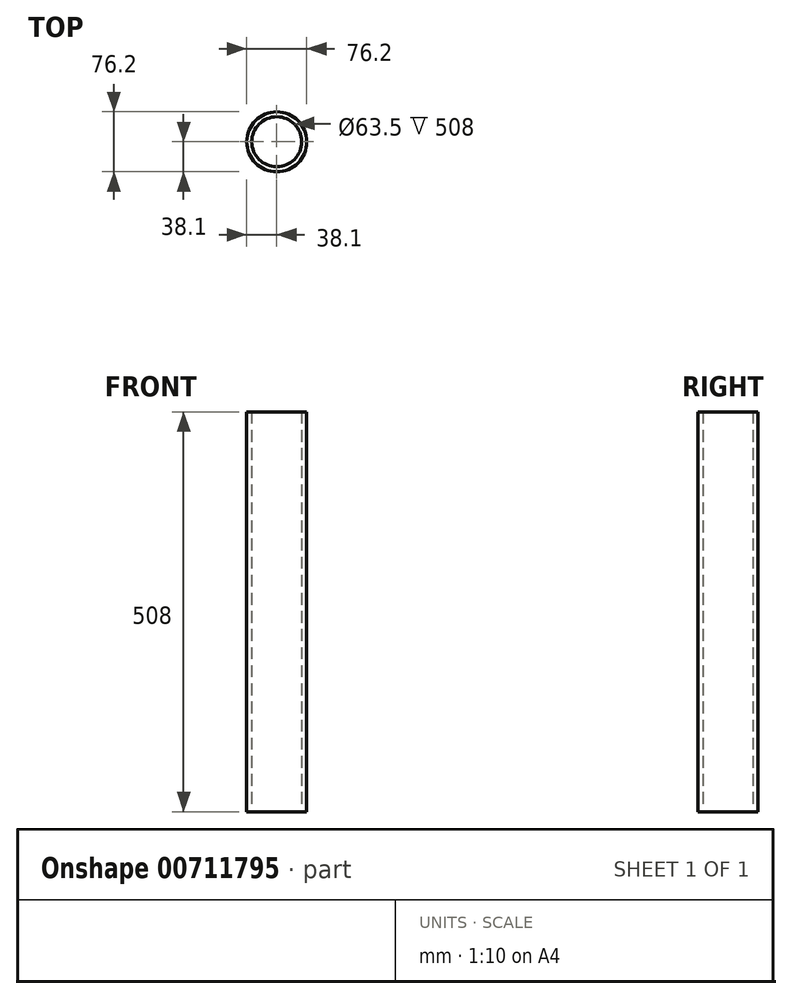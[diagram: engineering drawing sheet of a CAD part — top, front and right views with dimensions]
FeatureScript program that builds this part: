
annotation { "Feature Type Name" : "Feature", "Feature Type Description" : "" }
export const myFeature = defineFeature(function(context is Context, id is Id, definition is map)
    precondition{}
    {
        {
            var Q0;
            Q0=qCreatedBy(makeId("Top.planeOp"),FACE);
            var sketch = newSketch(context, id + "F0", { "sketchPlane" : qUnion([Q0])});
            skCircle(sketch, "E0", {"center": v(0, 0) * mm, "radius": 38.1 * mm});
            skCircle(sketch, "E1", {"center": v(0, 0) * mm, "radius": 31.75 * mm});
            skSolve(sketch);
        }
        {
            var Q0;
            Q0 = qSketchRegion(id + "F0", true);
            extrude(context, id + "F1", {"entities" : qUnion([Q0]), "endBound" : BoundingType.SYMMETRIC, "depth" : 508 * mm, "offsetDistance" : 25.4 * mm});
        }
    });
